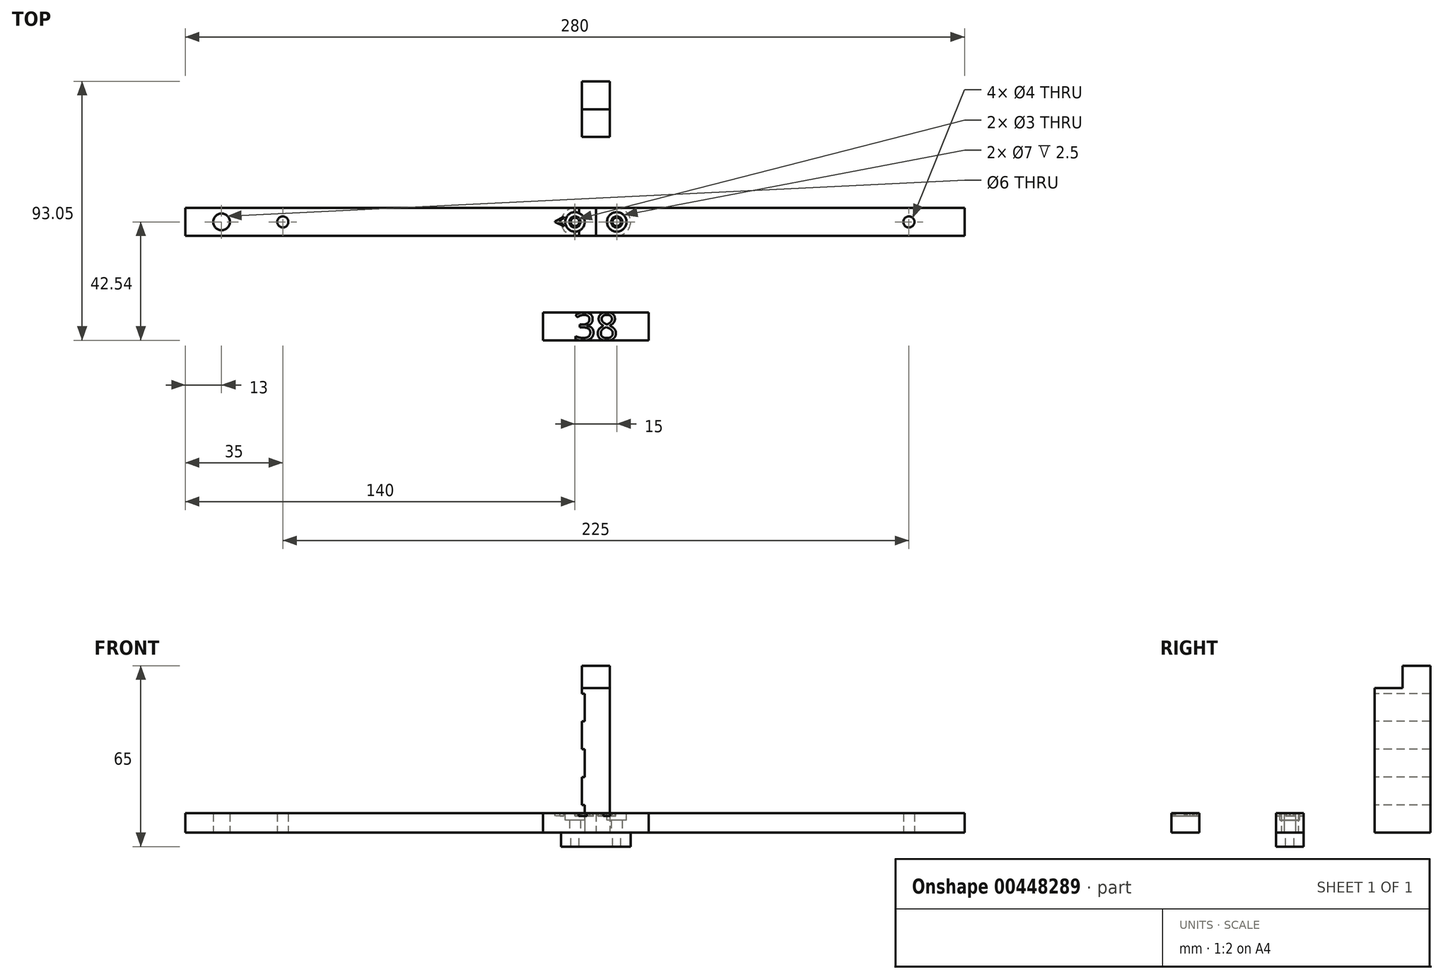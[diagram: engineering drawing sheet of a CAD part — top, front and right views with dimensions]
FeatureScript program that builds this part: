
annotation { "Feature Type Name" : "Feature", "Feature Type Description" : "" }
export const myFeature = defineFeature(function(context is Context, id is Id, definition is map)
    precondition{}
    {
        {
            var Q0;
            Q0=qCreatedBy(makeId("Top.planeOp"),FACE);
            var sketch = newSketch(context, id + "F0", { "sketchPlane" : qUnion([Q0])});
            skLineSegment(sketch, "E0.bottom", {"start": v(132.5, 5) * mm, "end": v(-140, 5) * mm});
            skLineSegment(sketch, "E0.top", {"start": v(132.5, -5) * mm, "end": v(-140, -5) * mm});
            skPoint(sketch, "E0.middle", {"position": v(0, 0) * mm});
            skLineSegment(sketch, "E1", {"start": v(0, 0) * mm, "end": v(-7.5, 0) * mm, "construction": true});
            skLineSegment(sketch, "E2", {"start": v(-7.5, 0) * mm, "end": v(-112.5, 0) * mm, "construction": true});
            skLineSegment(sketch, "E3", {"start": v(0, 0) * mm, "end": v(7.5, 0) * mm, "construction": true});
            skLineSegment(sketch, "E4", {"start": v(7.5, 0) * mm, "end": v(112.5, 0) * mm, "construction": true});
            skLineSegment(sketch, "E5", {"start": v(112.5, 0) * mm, "end": v(132.5, 0) * mm, "construction": true});
            skLineSegment(sketch, "E6", {"start": v(-112.5, 0) * mm, "end": v(-147.5, 0) * mm, "construction": true});
            skLineSegment(sketch, "E7", {"start": v(132.5, 0) * mm, "end": v(132.5, 5) * mm});
            skLineSegment(sketch, "E8", {"start": v(132.5, 0) * mm, "end": v(132.5, -5) * mm});
            skLineSegment(sketch, "E9", {"start": v(-147.5, 0) * mm, "end": v(-147.5, -5) * mm});
            skLineSegment(sketch, "E10", {"start": v(-140, -5) * mm, "end": v(-147.5, -5) * mm});
            skLineSegment(sketch, "E11", {"start": v(-140, 5) * mm, "end": v(-147.5, 5) * mm});
            skLineSegment(sketch, "E12", {"start": v(-147.5, 5) * mm, "end": v(-147.5, 0) * mm});
            skCircle(sketch, "E13", {"center": v(-112.5, 0) * mm, "radius": 2 * mm});
            skCircle(sketch, "E14", {"center": v(-7.5, 0) * mm, "radius": 2 * mm});
            skCircle(sketch, "E15", {"center": v(7.5, 0) * mm, "radius": 2 * mm});
            skCircle(sketch, "E16", {"center": v(112.5, 0) * mm, "radius": 2 * mm});
            skLineSegment(sketch, "E17", {"start": v(-147.5, 0) * mm, "end": v(-134.5, 0) * mm, "construction": true});
            skCircle(sketch, "E18", {"center": v(-134.5, 0) * mm, "radius": 3 * mm});
            skLineSegment(sketch, "E19", {"start": v(0, 0) * mm, "end": v(0, -5) * mm});
            skLineSegment(sketch, "E20", {"start": v(0, 0) * mm, "end": v(0, 5) * mm});
            skSolve(sketch);
        }
        {
            var Q0;
            Q0=makeQuery(id+"F0.imprint","IMPRINT",FACE,{"disambiguationData":[TD([[makeQuery(id+"F0.imprint","IMPRINT",EDGE,{"derivedFrom":sQuery(id+"F0.wireOp",EDGE,"E9")}),1.0]])]});
            extrude(context, id + "F1", {"entities" : qUnion([Q0]), "depth" : 7 * mm});
        }
        {
            var Q0;
            {var subQ0=sQuery(id+"F0.wireOp",EDGE,"E7");Q0=makeQuery(id+"F0.imprint","IMPRINT",FACE,{"disambiguationData":[TD([[makeQuery(id+"F0.imprint","IMPRINT",EDGE,{"derivedFrom":subQ0}),1.0]])]});}
            extrude(context, id + "F2", {"entities" : qUnion([Q0]), "depth" : 7 * mm});
        }
        {
            var Q0;
            Q0=makeQuery(id+"F1.opExtrude","CAP_FACE",FACE,{"disambiguationData":[OSD([sQuery(id+"F0.wireOp",EDGE,"E0.bottom"),sQuery(id+"F0.wireOp",EDGE,"E0.top"),sQuery(id+"F0.wireOp",EDGE,"E9"),sQuery(id+"F0.wireOp",EDGE,"E10"),sQuery(id+"F0.wireOp",EDGE,"E11"),sQuery(id+"F0.wireOp",EDGE,"E12"),sQuery(id+"F0.wireOp",EDGE,"E13"),sQuery(id+"F0.wireOp",EDGE,"E14"),sQuery(id+"F0.wireOp",EDGE,"E18"),sQuery(id+"F0.wireOp",EDGE,"E19"),sQuery(id+"F0.wireOp",EDGE,"E20")])],"isStart":false});
            var sketch = newSketch(context, id + "F3", { "sketchPlane" : qUnion([Q0])});
            skCircle(sketch, "E21", {"center": v(-7.5, 0) * mm, "radius": 3.5 * mm});
            skSolve(sketch);
        }
        {
            var Q0;
            Q0 = qSketchRegion(id + "F3", true);
            extrude(context, id + "F4", {"entities" : qUnion([Q0]), "operationType" : NewBodyOperationType.REMOVE, "oppositeDirection" : true, "depth" : 2.5 * mm});
        }
        {
            var Q0;
            Q0=makeQuery(id+"F2.opExtrude","CAP_FACE",FACE,{"disambiguationData":[OSD([sQuery(id+"F0.wireOp",EDGE,"E0.bottom"),sQuery(id+"F0.wireOp",EDGE,"E0.top"),sQuery(id+"F0.wireOp",EDGE,"E7"),sQuery(id+"F0.wireOp",EDGE,"E8"),sQuery(id+"F0.wireOp",EDGE,"E15"),sQuery(id+"F0.wireOp",EDGE,"E16"),sQuery(id+"F0.wireOp",EDGE,"E19"),sQuery(id+"F0.wireOp",EDGE,"E20")])],"isStart":false});
            var sketch = newSketch(context, id + "F5", { "sketchPlane" : qUnion([Q0])});
            skCircle(sketch, "E22", {"center": v(7.5, 0) * mm, "radius": 3.5 * mm});
            skSolve(sketch);
        }
        {
            var Q0;
            Q0=makeQuery(id+"F5.imprint","IMPRINT",FACE,{"disambiguationData":[TD([[makeQuery(id+"F5.imprint","IMPRINT",EDGE,{"derivedFrom":sQuery(id+"F5.wireOp",EDGE,"E22")}),1.0]])]});
            extrude(context, id + "F6", {"entities" : qUnion([Q0]), "operationType" : NewBodyOperationType.REMOVE, "oppositeDirection" : true, "depth" : 2.5 * mm});
        }
        {
            var Q0;
            Q0=qCreatedBy(makeId("Top.planeOp"),FACE);
            var sketch = newSketch(context, id + "F7", { "sketchPlane" : qUnion([Q0])});
            skLineSegment(sketch, "E23.0.0", {"start": v(0, -5) * mm, "end": v(-7.5, -5) * mm});
            skLineSegment(sketch, "E23.0.1", {"start": v(-147.5, -5) * mm, "end": v(-147.5, 5) * mm});
            skLineSegment(sketch, "E23.0.2", {"start": v(-7.5, 5) * mm, "end": v(0, 5) * mm});
            skLineSegment(sketch, "E24.0", {"start": v(7.5, -5) * mm, "end": v(0, -5) * mm});
            skLineSegment(sketch, "E25.0", {"start": v(7.5, 5) * mm, "end": v(0, 5) * mm});
            skCircle(sketch, "E26", {"center": v(-7.5, 0) * mm, "radius": 1.5 * mm});
            skCircle(sketch, "E27", {"center": v(7.5, 0) * mm, "radius": 1.5 * mm});
            skArc(sketch, "E28", {"start": v(-7.5, 5) * mm, "mid": v(-12.5, 0) * mm, "end": v(-7.5, -5) * mm});
            skArc(sketch, "E29", {"start": v(7.5, -5) * mm, "mid": v(12.5, 0) * mm, "end": v(7.5, 5) * mm});
            skPoint(sketch, "E30.orphan", {"position": v(132.5, 5) * mm});
            skPoint(sketch, "E31.orphan", {"position": v(132.5, -5) * mm});
            skSolve(sketch);
        }
        {
            var Q0;
            Q0=makeQuery(id+"F7.imprint","IMPRINT",FACE,{"disambiguationData":[TD([[makeQuery(id+"F7.imprint","IMPRINT",EDGE,{"derivedFrom":sQuery(id+"F7.wireOp",EDGE,"E23.0.0")}),-1.0]])]});
            extrude(context, id + "F8", {"entities" : qUnion([Q0]), "oppositeDirection" : true, "depth" : 5 * mm});
        }
        {
            var Q0;
            Q0=qCreatedBy(makeId("Top.planeOp"),FACE);
            var sketch = newSketch(context, id + "F9", { "sketchPlane" : qUnion([Q0])});
            skLineSegment(sketch, "E32.bottom", {"start": v(-5, 50.51) * mm, "end": v(5, 50.51) * mm});
            skLineSegment(sketch, "E32.top", {"start": v(-5, 30.51) * mm, "end": v(5, 30.51) * mm});
            skLineSegment(sketch, "E32.left", {"start": v(-5, 50.51) * mm, "end": v(-5, 30.51) * mm});
            skLineSegment(sketch, "E32.right", {"start": v(5, 50.51) * mm, "end": v(5, 30.51) * mm});
            skPoint(sketch, "E32.middle", {"position": v(0, 40.51) * mm});
            skSolve(sketch);
        }
        {
            var Q0;
            Q0=makeQuery(id+"F9.imprint","IMPRINT",FACE,{"disambiguationData":[TD([[makeQuery(id+"F9.imprint","IMPRINT",EDGE,{"derivedFrom":sQuery(id+"F9.wireOp",EDGE,"E32.bottom")}),-1.0]])]});
            extrude(context, id + "F10", {"entities" : qUnion([Q0]), "depth" : 60 * mm});
        }
        {
            var Q0;
            Q0=makeQuery(id+"F10.opExtrude","SWEPT_FACE",FACE,{"disambiguationData":[OSD([sQuery(id+"F9.wireOp",EDGE,"E32.left")])]});
            var sketch = newSketch(context, id + "F11", { "sketchPlane" : qUnion([Q0])});
            skLineSegment(sketch, "E33", {"start": v(-40.51, 60) * mm, "end": v(-40.51, 52) * mm});
            skLineSegment(sketch, "E34", {"start": v(-40.51, 52) * mm, "end": v(-30.51, 52) * mm});
            skLineSegment(sketch, "E35", {"start": v(-30.51, 52) * mm, "end": v(-30.51, 60) * mm});
            skLineSegment(sketch, "E36", {"start": v(-30.51, 60) * mm, "end": v(-40.51, 60) * mm});
            skSolve(sketch);
        }
        {
            var Q0;
            Q0=makeQuery(id+"F11.imprint","IMPRINT",FACE,{"disambiguationData":[TD([[makeQuery(id+"F11.imprint","IMPRINT",EDGE,{"derivedFrom":sQuery(id+"F11.wireOp",EDGE,"E33")}),1.0]])]});
            extrude(context, id + "F12", {"entities" : qUnion([Q0]), "operationType" : NewBodyOperationType.REMOVE, "endBound" : BoundingType.THROUGH_ALL, "oppositeDirection" : true, "depth" : 25 * mm});
        }
        {
            var Q0;
            Q0=qCreatedBy(makeId("Top.planeOp"),FACE);
            var sketch = newSketch(context, id + "F13", { "sketchPlane" : qUnion([Q0])});
            skLineSegment(sketch, "E37.bottom", {"start": v(19, -32.54) * mm, "end": v(-19, -32.54) * mm});
            skLineSegment(sketch, "E37.top", {"start": v(19, -42.54) * mm, "end": v(-19, -42.54) * mm});
            skLineSegment(sketch, "E37.left", {"start": v(19, -32.54) * mm, "end": v(19, -42.54) * mm});
            skLineSegment(sketch, "E37.right", {"start": v(-19, -32.54) * mm, "end": v(-19, -42.54) * mm});
            skPoint(sketch, "E37.middle", {"position": v(0, -37.54) * mm});
            skSolve(sketch);
        }
        {
            var Q0;
            Q0=makeQuery(id+"F13.imprint","IMPRINT",FACE,{"disambiguationData":[TD([[makeQuery(id+"F13.imprint","IMPRINT",EDGE,{"derivedFrom":sQuery(id+"F13.wireOp",EDGE,"E37.bottom")}),1.0]])]});
            extrude(context, id + "F14", {"entities" : qUnion([Q0]), "depth" : 7 * mm});
        }
        {
            var Q0;
            Q0=makeQuery(id+"F10.opExtrude","SWEPT_FACE",FACE,{"disambiguationData":[OSD([sQuery(id+"F9.wireOp",EDGE,"E32.left")])]});
            var sketch = newSketch(context, id + "F15", { "sketchPlane" : qUnion([Q0])});
            skLineSegment(sketch, "E38", {"start": v(-50.51, 0) * mm, "end": v(-50.51, 10) * mm, "construction": true});
            skLineSegment(sketch, "E39", {"start": v(-50.51, 10) * mm, "end": v(-50.51, 20) * mm, "construction": true});
            skLineSegment(sketch, "E40", {"start": v(-50.51, 20) * mm, "end": v(-50.51, 30) * mm, "construction": true});
            skLineSegment(sketch, "E41", {"start": v(-50.51, 30) * mm, "end": v(-50.51, 40) * mm, "construction": true});
            skLineSegment(sketch, "E42", {"start": v(-50.51, 40) * mm, "end": v(-50.51, 50) * mm, "construction": true});
            skLineSegment(sketch, "E43", {"start": v(-50.51, 50) * mm, "end": v(-50.51, 60) * mm, "construction": true});
            skLineSegment(sketch, "E44", {"start": v(-50.51, 10) * mm, "end": v(-30.51, 10) * mm});
            skLineSegment(sketch, "E45", {"start": v(-50.51, 20) * mm, "end": v(-30.51, 20) * mm});
            skLineSegment(sketch, "E46", {"start": v(-50.51, 30) * mm, "end": v(-30.51, 30) * mm});
            skLineSegment(sketch, "E47", {"start": v(-50.51, 40) * mm, "end": v(-30.51, 40) * mm});
            skLineSegment(sketch, "E48", {"start": v(-50.51, 50) * mm, "end": v(-30.51, 50) * mm});
            skSolve(sketch);
        }
        {
            var Q0;
            Q0 = qSketchRegion(id + "F15", true);
            var Q1;
            {var subQ0=sQuery(id+"F15.wireOp",EDGE,"E47");Q1=makeQuery(id+"F15.imprint","IMPRINT",FACE,{"disambiguationData":[TD([[makeQuery(id+"F15.imprint","IMPRINT",EDGE,{"derivedFrom":subQ0}),1.0]])]});}
            var Q2;
            {var subQ0=sQuery(id+"F15.wireOp",EDGE,"E45");Q2=makeQuery(id+"F15.imprint","IMPRINT",FACE,{"disambiguationData":[TD([[makeQuery(id+"F15.imprint","IMPRINT",EDGE,{"derivedFrom":subQ0}),1.0]])]});}
            var Q3;
            {var subQ0=sQuery(id+"F15.wireOp",EDGE,"E44");Q3=makeQuery(id+"F15.imprint","IMPRINT",FACE,{"disambiguationData":[TD([[makeQuery(id+"F15.imprint","IMPRINT",EDGE,{"derivedFrom":subQ0}),-1.0]])]});}
            extrude(context, id + "F16", {"entities" : qUnion([Q0, Q1, Q2, Q3]), "operationType" : NewBodyOperationType.REMOVE, "oppositeDirection" : true, "depth" : 1 * mm});
        }
        {
            var Q0;
            Q0=makeQuery(id+"F14.opExtrude","CAP_FACE",FACE,{"disambiguationData":[OSD([sQuery(id+"F13.wireOp",EDGE,"E37.bottom"),sQuery(id+"F13.wireOp",EDGE,"E37.top"),sQuery(id+"F13.wireOp",EDGE,"E37.left"),sQuery(id+"F13.wireOp",EDGE,"E37.right")])],"isStart":false});
            var sketch = newSketch(context, id + "F17", { "sketchPlane" : qUnion([Q0])});
            skText(sketch, "E49", { "text": "38", "fontName": "OpenSans-Regular.ttf"});
            const initialGuessF17  = {"E49": [-0.00797, -0.04254, 1, 0, 0.01]};
            skSetInitialGuess(sketch, initialGuessF17);
            skSolve(sketch);
        }
        {
            var Q0;
            {var subQ4=sQuery(id+"F17.wireOp",EDGE,"E49.sketch_text.stroke-29");Q0=makeQuery(id+"F17.imprint","IMPRINT",FACE,{"disambiguationData":[TD([[makeQuery(id+"F17.imprint","IMPRINT",EDGE,{"derivedFrom":subQ4}),-1.0]])]});}
            var Q1;
            Q1=makeQuery(id+"F17.imprint","IMPRINT",FACE,{"disambiguationData":[TD([[makeQuery(id+"F17.imprint","IMPRINT",EDGE,{"derivedFrom":sQuery(id+"F17.wireOp",EDGE,"E49.sketch_text.stroke-0")}),-1.0]])]});
            extrude(context, id + "F18", {"entities" : qUnion([Q0, Q1]), "operationType" : NewBodyOperationType.REMOVE, "oppositeDirection" : true, "depth" : 1 * mm});
        }
        {
            var Q0;
            Q0=makeQuery(id+"F1.opExtrude","CAP_FACE",FACE,{"disambiguationData":[OSD([sQuery(id+"F0.wireOp",EDGE,"E0.bottom"),sQuery(id+"F0.wireOp",EDGE,"E0.top"),sQuery(id+"F0.wireOp",EDGE,"E9"),sQuery(id+"F0.wireOp",EDGE,"E10"),sQuery(id+"F0.wireOp",EDGE,"E11"),sQuery(id+"F0.wireOp",EDGE,"E12"),sQuery(id+"F0.wireOp",EDGE,"E13"),sQuery(id+"F0.wireOp",EDGE,"E14"),sQuery(id+"F0.wireOp",EDGE,"E18"),sQuery(id+"F0.wireOp",EDGE,"E19"),sQuery(id+"F0.wireOp",EDGE,"E20")])],"isStart":false});
            var sketch = newSketch(context, id + "F19", { "sketchPlane" : qUnion([Q0])});
            skLineSegment(sketch, "E50", {"start": v(-147.5, -5) * mm, "end": v(-7.5, -5) * mm, "construction": true});
            skLineSegment(sketch, "E51", {"start": v(-7.5, -5) * mm, "end": v(-7.5, 5) * mm});
            skLineSegment(sketch, "E52", {"start": v(-7.5, 5) * mm, "end": v(-6, 5) * mm});
            skLineSegment(sketch, "E53", {"start": v(-6, 5) * mm, "end": v(-6, -5) * mm});
            skLineSegment(sketch, "E54", {"start": v(-6, -5) * mm, "end": v(-7.5, -5) * mm});
            skText(sketch, "E55", { "text": "<", "fontName": "OpenSans-Regular.ttf"});
            const initialGuessF19  = {"E55": [-0.01505, -0.00234, 1, 0, 0.00495]};
            skSetInitialGuess(sketch, initialGuessF19);
            skSolve(sketch);
        }
        {
            var Q0;
            Q0 = qSketchRegion(id + "F19", true);
            extrude(context, id + "F20", {"entities" : qUnion([Q0]), "operationType" : NewBodyOperationType.REMOVE, "oppositeDirection" : true, "depth" : 1 * mm});
        }
        {
            var Q0;
            {var subQ0=sQuery(id+"F0.wireOp",EDGE,"E11");var subQ1=sQuery(id+"F0.wireOp",EDGE,"E0.bottom");var subQ2=sQuery(id+"F19.wireOp",EDGE,"E51");Q0=makeQuery(id+"F20.boolean.opBoolean","COPY",EDGE,{"disambiguationData":[TD([makeQuery(id+"F1.opExtrude","SWEPT_FACE",FACE,{"disambiguationData":[OSD([subQ1,subQ0])]})])],"derivedFrom":makeQuery(id+"F20.opExtrude","CAP_EDGE",EDGE,{"disambiguationData":[OSD([subQ2])],"isStart":true})});}
            var Q1;
            {var subQ0=sQuery(id+"F0.wireOp",EDGE,"E11");var subQ1=sQuery(id+"F0.wireOp",EDGE,"E0.bottom");var subQ2=sQuery(id+"F19.wireOp",EDGE,"E53");Q1=makeQuery(id+"F20.boolean.opBoolean","COPY",EDGE,{"disambiguationData":[TD([makeQuery(id+"F1.opExtrude","SWEPT_FACE",FACE,{"disambiguationData":[OSD([subQ1,subQ0])]})])],"derivedFrom":makeQuery(id+"F20.opExtrude","CAP_EDGE",EDGE,{"disambiguationData":[OSD([subQ2])],"isStart":true})});}
            var Q2;
            {var subQ0=sQuery(id+"F0.wireOp",EDGE,"E10");var subQ1=sQuery(id+"F0.wireOp",EDGE,"E0.top");var subQ2=sQuery(id+"F19.wireOp",EDGE,"E51");Q2=makeQuery(id+"F20.boolean.opBoolean","COPY",EDGE,{"disambiguationData":[TD([makeQuery(id+"F1.opExtrude","SWEPT_FACE",FACE,{"disambiguationData":[OSD([subQ1,subQ0])]})])],"derivedFrom":makeQuery(id+"F20.opExtrude","CAP_EDGE",EDGE,{"disambiguationData":[OSD([subQ2])],"isStart":true})});}
            var Q3;
            {var subQ0=sQuery(id+"F0.wireOp",EDGE,"E10");var subQ1=sQuery(id+"F0.wireOp",EDGE,"E0.top");var subQ2=sQuery(id+"F19.wireOp",EDGE,"E53");Q3=makeQuery(id+"F20.boolean.opBoolean","COPY",EDGE,{"disambiguationData":[TD([makeQuery(id+"F1.opExtrude","SWEPT_FACE",FACE,{"disambiguationData":[OSD([subQ1,subQ0])]})])],"derivedFrom":makeQuery(id+"F20.opExtrude","CAP_EDGE",EDGE,{"disambiguationData":[OSD([subQ2])],"isStart":true})});}
            fillet(context, id + "F21", {"entities" : qUnion([Q0, Q1, Q2, Q3]), "radius" : .5 * mm, "tangentPropagation" : true, "allowEdgeOverflow" : false});
        }
        {
            var Q0;
            Q0=makeQuery(id+"F20.boolean.opBoolean","COPY",EDGE,{"derivedFrom":makeQuery(id+"F20.opExtrude","SWEPT_EDGE",EDGE,{"disambiguationData":[OSD([sQuery(id+"F19.wireOp",EDGE,"E55.sketch_text.stroke-4"),sQuery(id+"F19.wireOp",EDGE,"E55.sketch_text.stroke-5")])]})});
            fillet(context, id + "F22", {"entities" : qUnion([Q0]), "radius" : .8 * mm, "tangentPropagation" : true, "allowEdgeOverflow" : false});
        }
    });
